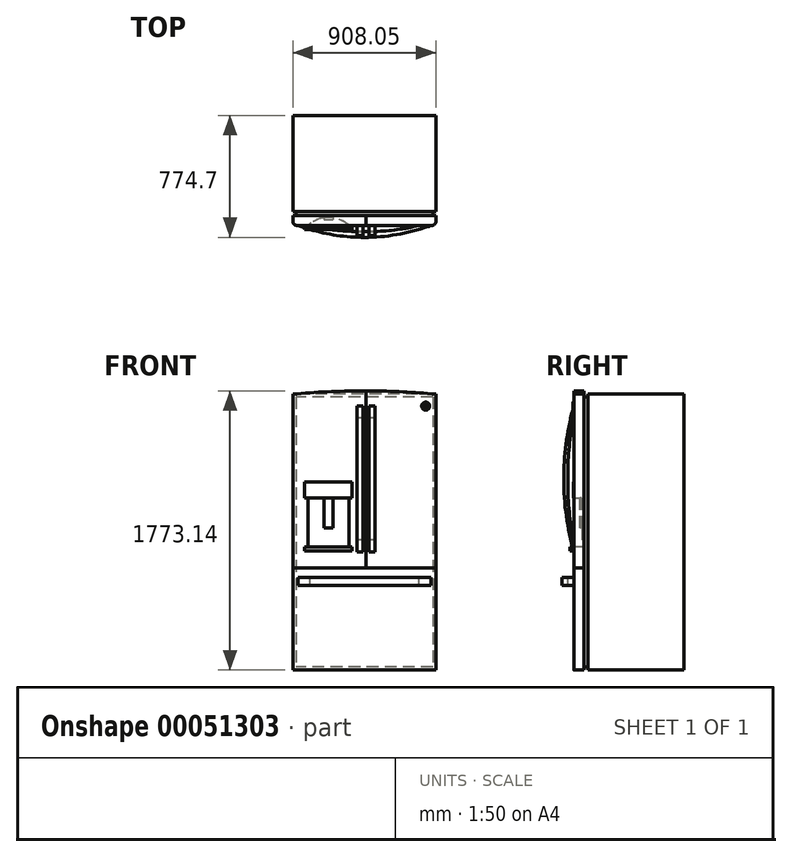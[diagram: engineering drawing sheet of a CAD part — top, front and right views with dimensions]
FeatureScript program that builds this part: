
annotation { "Feature Type Name" : "Feature", "Feature Type Description" : "" }
export const myFeature = defineFeature(function(context is Context, id is Id, definition is map)
    precondition{}
    {
        {
            var Q0;
            Q0=qCreatedBy(makeId("Front.planeOp"),FACE);
            var sketch = newSketch(context, id + "F0", { "sketchPlane" : qUnion([Q0])});
            skLineSegment(sketch, "E0.bottom", {"start": v(-463.95, 1156.1) * mm, "end": v(444.1, 1156.1) * mm, "construction": true});
            skLineSegment(sketch, "E0.top", {"start": v(-463.95, -596.5) * mm, "end": v(444.1, -596.5) * mm});
            skLineSegment(sketch, "E0.left", {"start": v(-463.95, 1156.1) * mm, "end": v(-463.95, -596.5) * mm});
            skLineSegment(sketch, "E0.right", {"start": v(444.1, 1156.1) * mm, "end": v(444.1, -596.5) * mm});
            skLineSegment(sketch, "E1", {"start": v(-463.95, 51.2) * mm, "end": v(444.1, 51.2) * mm});
            skLineSegment(sketch, "E2.bottom", {"start": v(-368.7, 496.57) * mm, "end": v(-108.35, 496.57) * mm});
            skLineSegment(sketch, "E2.top", {"start": v(-368.7, 186.46) * mm, "end": v(-108.35, 186.46) * mm});
            skLineSegment(sketch, "E2.left", {"start": v(-368.7, 496.57) * mm, "end": v(-368.7, 186.46) * mm});
            skLineSegment(sketch, "E2.right", {"start": v(-108.35, 496.57) * mm, "end": v(-108.35, 186.46) * mm});
            skLineSegment(sketch, "E3.bottom", {"start": v(-267.1, 306.07) * mm, "end": v(-209.95, 306.07) * mm});
            skLineSegment(sketch, "E3.top", {"start": v(-267.1, 496.57) * mm, "end": v(-209.95, 496.57) * mm});
            skLineSegment(sketch, "E3.left", {"start": v(-267.1, 306.07) * mm, "end": v(-267.1, 496.57) * mm});
            skLineSegment(sketch, "E3.right", {"start": v(-209.95, 306.07) * mm, "end": v(-209.95, 496.57) * mm});
            skLineSegment(sketch, "E4.bottom", {"start": v(-389.9, 598.17) * mm, "end": v(-87.14, 598.17) * mm});
            skLineSegment(sketch, "E4.top", {"start": v(-389.9, 496.57) * mm, "end": v(-87.14, 496.57) * mm});
            skLineSegment(sketch, "E4.left", {"start": v(-389.9, 598.17) * mm, "end": v(-389.9, 496.57) * mm});
            skLineSegment(sketch, "E4.right", {"start": v(-87.14, 598.17) * mm, "end": v(-87.14, 496.57) * mm});
            skLineSegment(sketch, "E5.bottom", {"start": v(-389.9, 161.06) * mm, "end": v(-87.14, 161.06) * mm});
            skLineSegment(sketch, "E5.top", {"start": v(-389.9, 186.46) * mm, "end": v(-87.14, 186.46) * mm});
            skLineSegment(sketch, "E5.left", {"start": v(-389.9, 161.06) * mm, "end": v(-389.9, 186.46) * mm});
            skLineSegment(sketch, "E5.right", {"start": v(-87.14, 161.06) * mm, "end": v(-87.14, 186.46) * mm});
            skArc(sketch, "E6", {"start": v(444.1, 1156.1) * mm, "mid": v(-9.92, 1176.64) * mm, "end": v(-463.95, 1156.1) * mm});
            skLineSegment(sketch, "E7", {"start": v(0, 51.2) * mm, "end": v(0, 1176.63) * mm});
            skSolve(sketch);
        }
        {
            var Q0;
            {var subQ4=sQuery(id+"F0.wireOp",EDGE,"E0.top");Q0=makeQuery(id+"F0.imprint","IMPRINT",FACE,{"disambiguationData":[TD([[makeQuery(id+"F0.imprint","IMPRINT",EDGE,{"derivedFrom":subQ4}),1.0]])]});}
            extrude(context, id + "F1", {"entities" : qUnion([Q0]), "oppositeDirection" : true, "depth" : 63.5 * mm});
        }
        {
            var Q0;
            Q0=makeQuery(id+"F0.imprint","IMPRINT",FACE,{"disambiguationData":[TD([[makeQuery(id+"F0.imprint","IMPRINT",EDGE,{"derivedFrom":sQuery(id+"F0.wireOp",EDGE,"E5.bottom")}),1.0]])]});
            var Q1;
            {var subQ4=sQuery(id+"F0.wireOp",EDGE,"E2.left");Q1=makeQuery(id+"F0.imprint","IMPRINT",FACE,{"disambiguationData":[TD([[makeQuery(id+"F0.imprint","IMPRINT",EDGE,{"derivedFrom":subQ4}),1.0]])]});}
            var Q2;
            Q2=makeQuery(id+"F0.imprint","IMPRINT",FACE,{"disambiguationData":[TD([[makeQuery(id+"F0.imprint","IMPRINT",EDGE,{"derivedFrom":sQuery(id+"F0.wireOp",EDGE,"E3.bottom")}),1.0]])]});
            var Q3;
            {var subQ5=sQuery(id+"F0.wireOp",EDGE,"E2.left");Q3=makeQuery(id+"F0.imprint","IMPRINT",FACE,{"disambiguationData":[TD([[makeQuery(id+"F0.imprint","IMPRINT",EDGE,{"derivedFrom":subQ5}),-1.0]])]});}
            var Q4;
            Q4=makeQuery(id+"F0.imprint","IMPRINT",FACE,{"disambiguationData":[TD([[makeQuery(id+"F0.imprint","IMPRINT",EDGE,{"derivedFrom":sQuery(id+"F0.wireOp",EDGE,"E4.bottom")}),-1.0]])]});
            extrude(context, id + "F2", {"entities" : qUnion([Q0, Q1, Q2, Q3, Q4]), "oppositeDirection" : true, "depth" : 63.5 * mm});
        }
        {
            var Q0;
            {var subQ0=sQuery(id+"F0.wireOp",EDGE,"E7");Q0=makeQuery(id+"F0.imprint","IMPRINT",FACE,{"disambiguationData":[TD([[makeQuery(id+"F0.imprint","IMPRINT",EDGE,{"derivedFrom":subQ0}),-1.0]])]});}
            extrude(context, id + "F3", {"entities" : qUnion([Q0]), "oppositeDirection" : true, "depth" : 63.5 * mm});
        }
        {
            var Q0;
            Q0=makeQuery(id+"F3.opExtrude","CAP_FACE",FACE,{"disambiguationData":[OSD([sQuery(id+"F0.wireOp",EDGE,"E0.right"),sQuery(id+"F0.wireOp",EDGE,"E1"),sQuery(id+"F0.wireOp",EDGE,"E6"),sQuery(id+"F0.wireOp",EDGE,"E7")])],"isStart":false});
            var sketch = newSketch(context, id + "F4", { "sketchPlane" : qUnion([Q0])});
            skLineSegment(sketch, "E8.bottom", {"start": v(-425.05, 1137.05) * mm, "end": v(444.9, 1137.05) * mm});
            skLineSegment(sketch, "E8.top", {"start": v(-425.05, -577.45) * mm, "end": v(444.9, -577.45) * mm});
            skLineSegment(sketch, "E8.left", {"start": v(-425.05, 1137.05) * mm, "end": v(-425.05, -577.45) * mm});
            skLineSegment(sketch, "E8.right", {"start": v(444.9, 1137.05) * mm, "end": v(444.9, -577.45) * mm});
            skSolve(sketch);
        }
        {
            var Q0;
            Q0=qSketchRegion(id+"F4",true);
            extrude(context, id + "F5", {"entities" : qUnion([Q0]), "depth" : 25.4 * mm});
        }
        {
            var Q0;
            Q0=makeQuery(id+"F5.opExtrude","CAP_FACE",FACE,{"disambiguationData":[OSD([sQuery(id+"F4.wireOp",EDGE,"E8.bottom"),sQuery(id+"F4.wireOp",EDGE,"E8.top"),sQuery(id+"F4.wireOp",EDGE,"E8.left"),sQuery(id+"F4.wireOp",EDGE,"E8.right")])],"isStart":false});
            var sketch = newSketch(context, id + "F6", { "sketchPlane" : qUnion([Q0])});
            skLineSegment(sketch, "E9.bottom", {"start": v(-444.1, 1156.1) * mm, "end": v(463.95, 1156.1) * mm});
            skLineSegment(sketch, "E9.top", {"start": v(-444.1, -596.5) * mm, "end": v(463.95, -596.5) * mm});
            skLineSegment(sketch, "E9.left", {"start": v(-444.1, 1156.1) * mm, "end": v(-444.1, -596.5) * mm});
            skLineSegment(sketch, "E9.right", {"start": v(463.95, 1156.1) * mm, "end": v(463.95, -596.5) * mm});
            skSolve(sketch);
        }
        {
            var Q0;
            Q0=qSketchRegion(id+"F6",true);
            extrude(context, id + "F7", {"entities" : qUnion([Q0]), "depth" : 609.6 * mm});
        }
        {
            var Q0;
            {var subQ4=sQuery(id+"F0.wireOp",EDGE,"E2.left");Q0=makeQuery(id+"F0.imprint","IMPRINT",FACE,{"disambiguationData":[TD([[makeQuery(id+"F0.imprint","IMPRINT",EDGE,{"derivedFrom":subQ4}),1.0]])]});}
            var Q1;
            Q1=makeQuery(id+"F0.imprint","IMPRINT",FACE,{"disambiguationData":[TD([[makeQuery(id+"F0.imprint","IMPRINT",EDGE,{"derivedFrom":sQuery(id+"F0.wireOp",EDGE,"E3.bottom")}),1.0]])]});
            extrude(context, id + "F8", {"entities" : qUnion([Q0, Q1]), "operationType" : NewBodyOperationType.REMOVE, "oppositeDirection" : true, "depth" : 50.8 * mm});
        }
        {
            var Q0;
            Q0=makeQuery(id+"F8.boolean.opBoolean","COPY",EDGE,{"derivedFrom":makeQuery(id+"F8.opExtrude","CAP_EDGE",EDGE,{"disambiguationData":[OSD([sQuery(id+"F0.wireOp",EDGE,"E2.right")])],"isStart":false})});
            var Q1;
            Q1=makeQuery(id+"F8.boolean.opBoolean","COPY",EDGE,{"derivedFrom":makeQuery(id+"F8.opExtrude","CAP_EDGE",EDGE,{"disambiguationData":[OSD([sQuery(id+"F0.wireOp",EDGE,"E2.left")])],"isStart":false})});
            fillet(context, id + "F9", {"entities" : qUnion([Q0, Q1]), "radius" : 190.5 * mm, "tangentPropagation" : true, "allowEdgeOverflow" : false});
        }
        {
            var Q0;
            Q0=makeQuery(id+"F0.imprint","IMPRINT",FACE,{"disambiguationData":[TD([[makeQuery(id+"F0.imprint","IMPRINT",EDGE,{"derivedFrom":sQuery(id+"F0.wireOp",EDGE,"E5.bottom")}),1.0]])]});
            extrude(context, id + "F10", {"entities" : qUnion([Q0]), "operationType" : NewBodyOperationType.ADD, "depth" : 25.4 * mm});
        }
        {
            var Q0;
            Q0=makeQuery(id+"F0.imprint","IMPRINT",FACE,{"disambiguationData":[TD([[makeQuery(id+"F0.imprint","IMPRINT",EDGE,{"derivedFrom":sQuery(id+"F0.wireOp",EDGE,"E4.bottom")}),-1.0]])]});
            extrude(context, id + "F11", {"entities" : qUnion([Q0]), "operationType" : NewBodyOperationType.ADD, "depth" : 3.17 * mm});
        }
        {
            var Q0;
            Q0=makeQuery(id+"F0.imprint","IMPRINT",FACE,{"disambiguationData":[TD([[makeQuery(id+"F0.imprint","IMPRINT",EDGE,{"derivedFrom":sQuery(id+"F0.wireOp",EDGE,"E3.bottom")}),1.0]])]});
            extrude(context, id + "F12", {"entities" : qUnion([Q0]), "operationType" : NewBodyOperationType.ADD, "endBound" : BoundingType.UP_TO_NEXT, "oppositeDirection" : true, "depth" : 12.7 * mm});
        }
        {
            var Q0;
            Q0=makeQuery(id+"F12.opExtrude","CAP_FACE",FACE,{"disambiguationData":[OSD([sQuery(id+"F0.wireOp",EDGE,"E3.bottom"),sQuery(id+"F0.wireOp",EDGE,"E3.left"),sQuery(id+"F0.wireOp",EDGE,"E3.right"),sQuery(id+"F0.wireOp",EDGE,"E4.top")])],"isStart":true});
            extrude(context, id + "F13", {"entities" : qUnion([Q0]), "operationType" : NewBodyOperationType.REMOVE, "oppositeDirection" : true, "depth" : 38.1 * mm});
        }
        {
            var Q0;
            {var subQ0=sQuery(id+"F0.wireOp",EDGE,"E7");Q0=makeQuery(id+"F0.imprint","IMPRINT",FACE,{"disambiguationData":[TD([[makeQuery(id+"F0.imprint","IMPRINT",EDGE,{"derivedFrom":subQ0}),-1.0]])]});}
            var sketch = newSketch(context, id + "F14", { "sketchPlane" : qUnion([Q0])});
            skLineSegment(sketch, "E10.bottom", {"start": v(-432.2, -8.49) * mm, "end": v(412.35, -8.49) * mm});
            skLineSegment(sketch, "E10.top", {"start": v(-432.2, -59.29) * mm, "end": v(412.35, -59.29) * mm});
            skLineSegment(sketch, "E10.left", {"start": v(-432.2, -8.49) * mm, "end": v(-432.2, -59.29) * mm});
            skLineSegment(sketch, "E10.right", {"start": v(412.35, -8.49) * mm, "end": v(412.35, -59.29) * mm});
            skLineSegment(sketch, "E11.bottom", {"start": v(57.15, 1079.9) * mm, "end": v(19.05, 1079.9) * mm});
            skLineSegment(sketch, "E11.top", {"start": v(57.15, 152.8) * mm, "end": v(19.05, 152.8) * mm});
            skLineSegment(sketch, "E11.left", {"start": v(57.15, 1079.9) * mm, "end": v(57.15, 152.8) * mm});
            skLineSegment(sketch, "E11.right", {"start": v(19.05, 1079.9) * mm, "end": v(19.05, 152.8) * mm});
            skLineSegment(sketch, "E12.bottom", {"start": v(-19.05, 152.8) * mm, "end": v(-57.15, 152.8) * mm});
            skLineSegment(sketch, "E12.top", {"start": v(-19.05, 1079.9) * mm, "end": v(-57.15, 1079.9) * mm});
            skLineSegment(sketch, "E12.left", {"start": v(-19.05, 152.8) * mm, "end": v(-19.05, 1079.9) * mm});
            skLineSegment(sketch, "E12.right", {"start": v(-57.15, 152.8) * mm, "end": v(-57.15, 1079.9) * mm});
            skSolve(sketch);
        }
        {
            var Q0;
            Q0=makeQuery(id+"F14.imprint","IMPRINT",FACE,{"disambiguationData":[TD([[makeQuery(id+"F14.imprint","IMPRINT",EDGE,{"derivedFrom":sQuery(id+"F14.wireOp",EDGE,"E10.bottom")}),-1.0]])]});
            extrude(context, id + "F15", {"entities" : qUnion([Q0]), "operationType" : NewBodyOperationType.ADD, "depth" : 76.2 * mm});
        }
        {
            var Q0;
            Q0=makeQuery(id+"F14.imprint","IMPRINT",FACE,{"disambiguationData":[TD([[makeQuery(id+"F14.imprint","IMPRINT",EDGE,{"derivedFrom":sQuery(id+"F14.wireOp",EDGE,"E11.bottom")}),1.0]])]});
            extrude(context, id + "F16", {"entities" : qUnion([Q0]), "operationType" : NewBodyOperationType.ADD, "depth" : 63.5 * mm});
        }
        {
            var Q0;
            Q0=makeQuery(id+"F14.imprint","IMPRINT",FACE,{"disambiguationData":[TD([[makeQuery(id+"F14.imprint","IMPRINT",EDGE,{"derivedFrom":sQuery(id+"F14.wireOp",EDGE,"E12.bottom")}),-1.0]])]});
            extrude(context, id + "F17", {"entities" : qUnion([Q0]), "operationType" : NewBodyOperationType.ADD, "depth" : 63.5 * mm});
        }
        {
            var Q0;
            Q0=makeQuery(id+"F15.opExtrude","SWEPT_FACE",FACE,{"disambiguationData":[OSD([sQuery(id+"F14.wireOp",EDGE,"E10.bottom")])]});
            var sketch = newSketch(context, id + "F18", { "sketchPlane" : qUnion([Q0])});
            skLineSegment(sketch, "E13.bottom", {"start": v(-356, 0) * mm, "end": v(336.15, 0) * mm});
            skLineSegment(sketch, "E13.top", {"start": v(-356, -38.1) * mm, "end": v(336.15, -38.1) * mm});
            skLineSegment(sketch, "E13.left", {"start": v(-356, 0) * mm, "end": v(-356, -38.1) * mm});
            skLineSegment(sketch, "E13.right", {"start": v(336.15, 0) * mm, "end": v(336.15, -38.1) * mm});
            skSolve(sketch);
        }
        {
            var Q0;
            Q0=qSketchRegion(id+"F18",true);
            extrude(context, id + "F19", {"entities" : qUnion([Q0]), "operationType" : NewBodyOperationType.REMOVE, "endBound" : BoundingType.THROUGH_ALL, "oppositeDirection" : true, "depth" : 25.4 * mm});
        }
        {
            var Q0;
            Q0=makeQuery(id+"F17.opExtrude","SWEPT_FACE",FACE,{"disambiguationData":[OSD([sQuery(id+"F14.wireOp",EDGE,"E12.right")])]});
            var sketch = newSketch(context, id + "F20", { "sketchPlane" : qUnion([Q0])});
            skLineSegment(sketch, "E14.bottom", {"start": v(0, 229) * mm, "end": v(38.1, 229) * mm});
            skLineSegment(sketch, "E14.top", {"start": v(0, 1003.7) * mm, "end": v(38.1, 1003.7) * mm});
            skLineSegment(sketch, "E14.left", {"start": v(0, 229) * mm, "end": v(0, 1003.7) * mm});
            skLineSegment(sketch, "E14.right", {"start": v(38.1, 229) * mm, "end": v(38.1, 1003.7) * mm});
            skSolve(sketch);
        }
        {
            var Q0;
            Q0=qSketchRegion(id+"F20",true);
            extrude(context, id + "F21", {"entities" : qUnion([Q0]), "operationType" : NewBodyOperationType.REMOVE, "oppositeDirection" : true, "depth" : 304.8 * mm});
        }
        {
            var Q0;
            Q0=makeQuery(id+"F16.opExtrude","SWEPT_FACE",FACE,{"disambiguationData":[OSD([sQuery(id+"F14.wireOp",EDGE,"E11.left")])]});
            var sketch = newSketch(context, id + "F22", { "sketchPlane" : qUnion([Q0])});
            skLineSegment(sketch, "E15.bottom", {"start": v(-38.1, 229) * mm, "end": v(0, 229) * mm});
            skLineSegment(sketch, "E15.top", {"start": v(-38.1, 1003.7) * mm, "end": v(0, 1003.7) * mm});
            skLineSegment(sketch, "E15.left", {"start": v(-38.1, 229) * mm, "end": v(-38.1, 1003.7) * mm});
            skLineSegment(sketch, "E15.right", {"start": v(0, 229) * mm, "end": v(0, 1003.7) * mm});
            skSolve(sketch);
        }
        {
            var Q0;
            Q0=makeQuery(id+"F22.imprint","IMPRINT",FACE,{"disambiguationData":[TD([[makeQuery(id+"F22.imprint","IMPRINT",EDGE,{"derivedFrom":sQuery(id+"F22.wireOp",EDGE,"E15.bottom")}),1.0]])]});
            extrude(context, id + "F23", {"entities" : qUnion([Q0]), "operationType" : NewBodyOperationType.REMOVE, "oppositeDirection" : true, "depth" : 50.8 * mm});
        }
        {
            var Q0;
            Q0=makeQuery(id+"F23.boolean.opBoolean","COPY",EDGE,{"derivedFrom":makeQuery(id+"F23.opExtrude","SWEPT_EDGE",EDGE,{"disambiguationData":[OSD([sQuery(id+"F22.wireOp",EDGE,"E15.top"),sQuery(id+"F22.wireOp",EDGE,"E15.left")])]})});
            var Q1;
            Q1=makeQuery(id+"F23.boolean.opBoolean","COPY",EDGE,{"derivedFrom":makeQuery(id+"F23.opExtrude","SWEPT_EDGE",EDGE,{"disambiguationData":[OSD([sQuery(id+"F22.wireOp",EDGE,"E15.bottom"),sQuery(id+"F22.wireOp",EDGE,"E15.left")])]})});
            var Q2;
            Q2=makeQuery(id+"F21.boolean.opBoolean","COPY",EDGE,{"derivedFrom":makeQuery(id+"F21.opExtrude","SWEPT_EDGE",EDGE,{"disambiguationData":[OSD([sQuery(id+"F20.wireOp",EDGE,"E14.bottom"),sQuery(id+"F20.wireOp",EDGE,"E14.right")])]})});
            var Q3;
            Q3=makeQuery(id+"F16.opExtrude","CAP_EDGE",EDGE,{"disambiguationData":[OSD([sQuery(id+"F14.wireOp",EDGE,"E11.bottom")])],"isStart":false});
            var Q4;
            Q4=makeQuery(id+"F17.opExtrude","CAP_EDGE",EDGE,{"disambiguationData":[OSD([sQuery(id+"F14.wireOp",EDGE,"E12.top")])],"isStart":false});
            var Q5;
            Q5=makeQuery(id+"F16.opExtrude","CAP_EDGE",EDGE,{"disambiguationData":[OSD([sQuery(id+"F14.wireOp",EDGE,"E11.top")])],"isStart":false});
            var Q6;
            Q6=makeQuery(id+"F17.opExtrude","CAP_EDGE",EDGE,{"disambiguationData":[OSD([sQuery(id+"F14.wireOp",EDGE,"E12.bottom")])],"isStart":false});
            var Q7;
            Q7=makeQuery(id+"F21.boolean.opBoolean","COPY",EDGE,{"derivedFrom":makeQuery(id+"F21.opExtrude","SWEPT_EDGE",EDGE,{"disambiguationData":[OSD([sQuery(id+"F20.wireOp",EDGE,"E14.top"),sQuery(id+"F20.wireOp",EDGE,"E14.right")])]})});
            fillet(context, id + "F24", {"entities" : qUnion([Q0, Q1, Q2, Q3, Q4, Q5, Q6, Q7]), "radius" : 1723.4 * mm, "tangentPropagation" : true, "allowEdgeOverflow" : false});
        }
        {
            var Q0;
            Q0=makeQuery(id+"F15.opExtrude","CAP_EDGE",EDGE,{"disambiguationData":[OSD([sQuery(id+"F14.wireOp",EDGE,"E10.left")])],"isStart":false});
            var Q1;
            Q1=makeQuery(id+"F15.opExtrude","CAP_EDGE",EDGE,{"disambiguationData":[OSD([sQuery(id+"F14.wireOp",EDGE,"E10.right")])],"isStart":false});
            var Q2;
            Q2=makeQuery(id+"F19.boolean.opBoolean","COPY",EDGE,{"derivedFrom":makeQuery(id+"F19.opExtrude","SWEPT_EDGE",EDGE,{"disambiguationData":[OSD([sQuery(id+"F18.wireOp",EDGE,"E13.top"),sQuery(id+"F18.wireOp",EDGE,"E13.right")])]})});
            var Q3;
            Q3=makeQuery(id+"F19.boolean.opBoolean","COPY",EDGE,{"derivedFrom":makeQuery(id+"F19.opExtrude","SWEPT_EDGE",EDGE,{"disambiguationData":[OSD([sQuery(id+"F18.wireOp",EDGE,"E13.top"),sQuery(id+"F18.wireOp",EDGE,"E13.left")])]})});
            fillet(context, id + "F25", {"entities" : qUnion([Q0, Q1, Q2, Q3]), "radius" : 1206.5 * mm, "tangentPropagation" : true, "allowEdgeOverflow" : false});
        }
        {
            var Q0;
            Q0=makeQuery(id+"F23.boolean.opBoolean","MERGE",FACE,{"derivedFrom":[makeQuery(id+"F3.opExtrude","CAP_FACE",FACE,{"disambiguationData":[OSD([sQuery(id+"F0.wireOp",EDGE,"E0.right"),sQuery(id+"F0.wireOp",EDGE,"E1"),sQuery(id+"F0.wireOp",EDGE,"E6"),sQuery(id+"F0.wireOp",EDGE,"E7")])],"isStart":true}),makeQuery(id+"F23.opExtrude","SWEPT_FACE",FACE,{"disambiguationData":[OSD([sQuery(id+"F22.wireOp",EDGE,"E15.right")])]})]});
            var sketch = newSketch(context, id + "F26", { "sketchPlane" : qUnion([Q0])});
            skCircle(sketch, "E16", {"center": v(379.68, 1079.9) * mm, "radius": 25.4 * mm});
            skSolve(sketch);
        }
        {
            var Q0;
            Q0=makeQuery(id+"F26.imprint","IMPRINT",FACE,{"disambiguationData":[TD([[makeQuery(id+"F26.imprint","IMPRINT",EDGE,{"derivedFrom":sQuery(id+"F26.wireOp",EDGE,"E16")}),1.0]])]});
            var Q1;
            Q1=sQuery(id+"F26.wireOp",EDGE,"E16");
            extrude(context, id + "F27", {"entities" : qUnion([Q0]), "surfaceEntities" : qUnion([Q1]), "depth" : 6.35 * mm});
        }
        {
            var Q0;
            Q0=makeQuery(id+"F27.opExtrude","CAP_EDGE",EDGE,{"disambiguationData":[OSD([sQuery(id+"F26.wireOp",EDGE,"E16")])],"isStart":false});
            fillet(context, id + "F28", {"entities" : qUnion([Q0]), "radius" : 3.17 * mm, "tangentPropagation" : true, "allowEdgeOverflow" : false});
        }
        {
            var Q0;
            Q0=makeQuery(id+"F27.opExtrude","CAP_FACE",FACE,{"disambiguationData":[OSD([sQuery(id+"F26.wireOp",EDGE,"E16")])],"isStart":false});
            var sketch = newSketch(context, id + "F29", { "sketchPlane" : qUnion([Q0])});
            skText(sketch, "E17", { "text": "GE", "fontName": "NotoSerif-BoldItalic.ttf"});
            const initialGuessF29  = {"E17": [0.36155, 1.07014, 1, 0, 0.01871]};
            skSetInitialGuess(sketch, initialGuessF29);
            skSolve(sketch);
        }
        {
            var Q0;
            Q0=qSketchRegion(id+"F29",true);
            extrude(context, id + "F30", {"entities" : qUnion([Q0]), "operationType" : NewBodyOperationType.REMOVE, "oppositeDirection" : true, "depth" : 3.17 * mm});
        }
        {
            var Q0;
            Q0=makeQuery(id+"F1.opExtrude","CAP_EDGE",EDGE,{"disambiguationData":[OSD([sQuery(id+"F0.wireOp",EDGE,"E0.right")])],"isStart":true});
            var Q1;
            Q1=makeQuery(id+"F3.opExtrude","CAP_EDGE",EDGE,{"disambiguationData":[OSD([sQuery(id+"F0.wireOp",EDGE,"E0.right")])],"isStart":true});
            var Q2;
            Q2=makeQuery(id+"F2.opExtrude","CAP_EDGE",EDGE,{"disambiguationData":[OSD([sQuery(id+"F0.wireOp",EDGE,"E0.left")])],"isStart":true});
            var Q3;
            Q3=makeQuery(id+"F1.opExtrude","CAP_EDGE",EDGE,{"disambiguationData":[OSD([sQuery(id+"F0.wireOp",EDGE,"E0.left")])],"isStart":true});
            fillet(context, id + "F31", {"entities" : qUnion([Q0, Q1, Q2, Q3]), "radius" : 25.4 * mm, "tangentPropagation" : true, "allowEdgeOverflow" : false});
        }
    });
